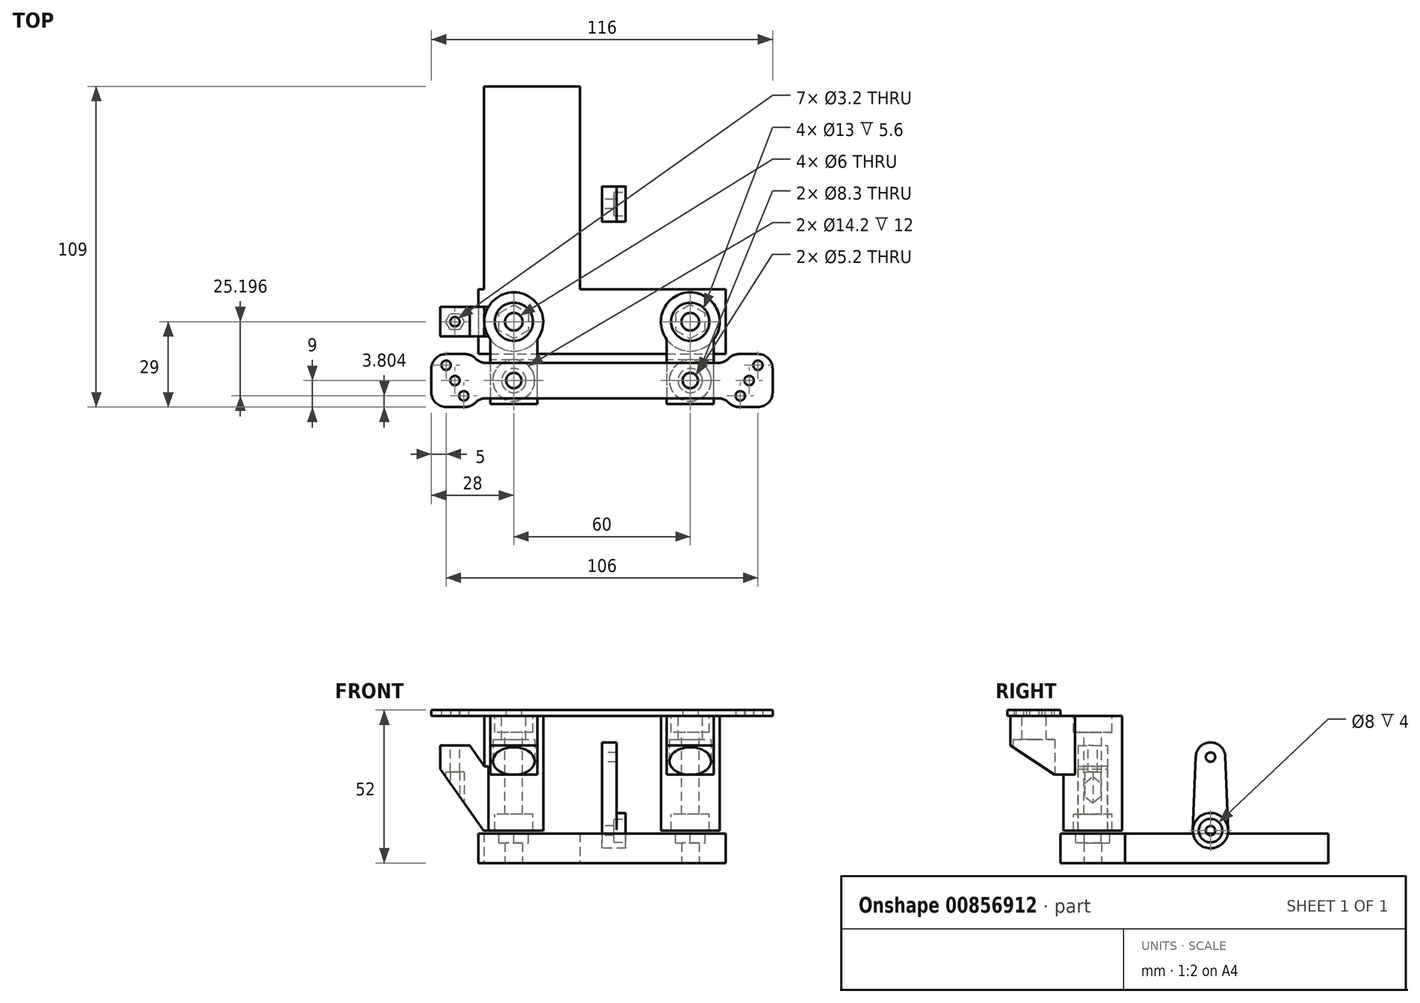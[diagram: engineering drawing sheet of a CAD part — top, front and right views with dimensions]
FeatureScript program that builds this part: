
annotation { "Feature Type Name" : "Feature", "Feature Type Description" : "" }
export const myFeature = defineFeature(function(context is Context, id is Id, definition is map)
    precondition{}
    {
        {
            var Q0;
            Q0=qCreatedBy(makeId("Top.planeOp"),FACE);
            var sketch = newSketch(context, id + "F0", { "sketchPlane" : qUnion([Q0])});
            skCircle(sketch, "E0", {"center": v(-30, 0) * mm, "radius": 3 * mm});
            skCircle(sketch, "E1", {"center": v(30, 0) * mm, "radius": 3 * mm});
            skLineSegment(sketch, "E2.bottom", {"start": v(-42, 11) * mm, "end": v(42, 11) * mm});
            skLineSegment(sketch, "E2.top", {"start": v(-42, -11) * mm, "end": v(42, -11) * mm});
            skLineSegment(sketch, "E2.left", {"start": v(-42, 11) * mm, "end": v(-42, -11) * mm});
            skLineSegment(sketch, "E2.right", {"start": v(42, 11) * mm, "end": v(42, -11) * mm});
            skPoint(sketch, "E2.middle", {"position": v(0, 0) * mm});
            skLineSegment(sketch, "E3", {"start": v(-30, 0) * mm, "end": v(30, 0) * mm, "construction": true});
            skSolve(sketch);
        }
        {
            var Q0;
            Q0 = qSketchRegion(id + "F0", true);
            extrude(context, id + "F1", {"entities" : qUnion([Q0]), "depth" : 10 * mm, "offsetDistance" : 25 * mm});
        }
        {
            var Q0;
            Q0=makeQuery(id+"F1.opExtrude","CAP_FACE",FACE,{"disambiguationData":[OSD([sQuery(id+"F0.wireOp",EDGE,"E0"),sQuery(id+"F0.wireOp",EDGE,"E1"),sQuery(id+"F0.wireOp",EDGE,"E2.bottom"),sQuery(id+"F0.wireOp",EDGE,"E2.top"),sQuery(id+"F0.wireOp",EDGE,"E2.left"),sQuery(id+"F0.wireOp",EDGE,"E2.right")])],"isStart":false});
            var sketch = newSketch(context, id + "F2", { "sketchPlane" : qUnion([Q0])});
            skCircle(sketch, "E4.cCircle", {"center": v(-30, 0) * mm, "radius": 5 * mm, "construction": true});
            skLineSegment(sketch, "E4.0", {"start": v(-25, 2.89) * mm, "end": v(-25, -2.89) * mm});
            skLineSegment(sketch, "E4.1", {"start": v(-25, -2.89) * mm, "end": v(-30, -5.77) * mm});
            skLineSegment(sketch, "E4.2", {"start": v(-30, -5.77) * mm, "end": v(-35, -2.89) * mm});
            skLineSegment(sketch, "E4.3", {"start": v(-35, -2.89) * mm, "end": v(-35, 2.89) * mm});
            skLineSegment(sketch, "E4.4", {"start": v(-35, 2.89) * mm, "end": v(-30, 5.77) * mm});
            skLineSegment(sketch, "E4.5", {"start": v(-30, 5.77) * mm, "end": v(-25, 2.89) * mm});
            skPoint(sketch, "E4.0.midPoint", {"position": v(-25, 0) * mm});
            skLineSegment(sketch, "E5", {"start": v(0, 0) * mm, "end": v(0, 13.19) * mm, "construction": true});
            skLineSegment(sketch, "E6.MirrorCS", {"start": v(25, -2.89) * mm, "end": v(30, -5.77) * mm});
            skLineSegment(sketch, "E7.MirrorCS", {"start": v(35, 2.89) * mm, "end": v(30, 5.77) * mm});
            skPoint(sketch, "E8.MirrorP", {"position": v(25, 0) * mm});
            skCircle(sketch, "E9.MirrorC", {"center": v(30, 0) * mm, "radius": 5 * mm, "construction": true});
            skLineSegment(sketch, "E10.MirrorCS", {"start": v(25, 2.89) * mm, "end": v(25, -2.89) * mm});
            skLineSegment(sketch, "E11.MirrorCS", {"start": v(30, -5.77) * mm, "end": v(35, -2.89) * mm});
            skLineSegment(sketch, "E12.MirrorCS", {"start": v(35, -2.89) * mm, "end": v(35, 2.89) * mm});
            skLineSegment(sketch, "E13.MirrorCS", {"start": v(30, 5.77) * mm, "end": v(25, 2.89) * mm});
            skSolve(sketch);
        }
        {
            var Q0;
            Q0 = qSketchRegion(id + "F2", true);
            extrude(context, id + "F3", {"entities" : qUnion([Q0]), "operationType" : NewBodyOperationType.REMOVE, "oppositeDirection" : true, "depth" : 3.2 * mm, "offsetDistance" : 25 * mm});
        }
        {
            var Q0;
            Q0=qCreatedBy(makeId("Front.planeOp"),FACE);
            var sketch = newSketch(context, id + "F4", { "sketchPlane" : qUnion([Q0])});
            skLineSegment(sketch, "E14", {"start": v(-30, 31.7) * mm, "end": v(-30, -19.85) * mm, "construction": true});
            skLineSegment(sketch, "E15", {"start": v(0, 0) * mm, "end": v(0, 44.27) * mm, "construction": true});
            skLineSegment(sketch, "E16.bottom", {"start": v(-40, 11) * mm, "end": v(-36.5, 11) * mm});
            skLineSegment(sketch, "E16.top", {"start": v(-40, 50) * mm, "end": v(-36.5, 50) * mm});
            skLineSegment(sketch, "E16.left", {"start": v(-40, 11) * mm, "end": v(-40, 50) * mm});
            skLineSegment(sketch, "E17.right", {"start": v(-36.5, 11) * mm, "end": v(-36.5, 16.6) * mm});
            skLineSegment(sketch, "E18", {"start": v(-33, 44.4) * mm, "end": v(-33, 16.6) * mm});
            skLineSegment(sketch, "E19.trimOffspring", {"start": v(-33, 16.6) * mm, "end": v(-36.5, 16.6) * mm});
            skLineSegment(sketch, "E20", {"start": v(-40, 30.5) * mm, "end": v(-16.74, 30.5) * mm, "construction": true});
            skLineSegment(sketch, "E21.MirrorCS", {"start": v(-33, 44.4) * mm, "end": v(-36.5, 44.4) * mm});
            skLineSegment(sketch, "E22.MirrorCS", {"start": v(-36.5, 50) * mm, "end": v(-36.5, 44.4) * mm});
            skSolve(sketch);
        }
        {
            var Q0;
            Q0=makeQuery(id+"F4.imprint","IMPRINT",FACE,{"disambiguationData":[TD([[makeQuery(id+"F4.imprint","IMPRINT",EDGE,{"derivedFrom":sQuery(id+"F4.wireOp",EDGE,"E16.bottom")}),1.0]])]});
            var Q1;
            Q1=sQuery(id+"F4.wireOp",EDGE,"E14");
            revolve(context, id + "F5", {"surfaceOperationType" : NewSurfaceOperationType.NEW, "entities" : qUnion([Q0]), "axis" : qUnion([Q1]), "revolveType" : RevolveType.FULL});
        }
        {
            var Q0;
            Q0=makeQuery(id+"F5.opRevolve","SWEPT_FACE",FACE,{"disambiguationData":[OSD([sQuery(id+"F4.wireOp",EDGE,"E16.top")])]});
            var sketch = newSketch(context, id + "F6", { "sketchPlane" : qUnion([Q0])});
            skArc(sketch, "E23.0", {"start": v(-38, -6) * mm, "mid": v(-30, -10) * mm, "end": v(-22, -6) * mm});
            skLineSegment(sketch, "E24", {"start": v(-38, -6) * mm, "end": v(-38, -28) * mm});
            skLineSegment(sketch, "E25", {"start": v(-38, -28) * mm, "end": v(-22, -28) * mm});
            skLineSegment(sketch, "E26", {"start": v(-22, -28) * mm, "end": v(-22, -6) * mm});
            skLineSegment(sketch, "E27", {"start": v(-30, 0) * mm, "end": v(-30, -20) * mm, "construction": true});
            skCircle(sketch, "E28", {"center": v(-30, -20) * mm, "radius": 4.15 * mm});
            skSolve(sketch);
        }
        {
            var Q0;
            Q0 = qSketchRegion(id + "F6", true);
            extrude(context, id + "F7", {"entities" : qUnion([Q0]), "operationType" : NewBodyOperationType.ADD, "oppositeDirection" : true, "depth" : 20 * mm, "offsetDistance" : 25 * mm});
        }
        {
            var Q0;
            Q0=makeQuery(id+"F7.opExtrude","CAP_EDGE",EDGE,{"disambiguationData":[OSD([sQuery(id+"F6.wireOp",EDGE,"E25")])],"isStart":false});
            chamfer(context, id + "F8", {"entities" : qUnion([Q0]), "chamferType" : ChamferType.TWO_OFFSETS, "width1" : 10 * mm, "oppositeDirection" : false, "width2" : 15 * mm, "tangentPropagation" : true});
        }
        {
            var Q0;
            Q0=makeQuery(id+"F7.opExtrude","CAP_FACE",FACE,{"disambiguationData":[OSD([sQuery(id+"F6.wireOp",EDGE,"E23.0"),sQuery(id+"F6.wireOp",EDGE,"E24"),sQuery(id+"F6.wireOp",EDGE,"E25"),sQuery(id+"F6.wireOp",EDGE,"E26"),sQuery(id+"F6.wireOp",EDGE,"E28")])],"isStart":false});
            var sketch = newSketch(context, id + "F9", { "sketchPlane" : qUnion([Q0])});
            skCircle(sketch, "E29.0", {"center": v(-30, 20) * mm, "radius": 4.15 * mm, "construction": true});
            skCircle(sketch, "E30.cCircle", {"center": v(-30, 20) * mm, "radius": 7.1 * mm});
            skLineSegment(sketch, "E30.0", {"start": v(-34.1, 27.1) * mm, "end": v(-25.9, 27.1) * mm, "construction": true});
            skLineSegment(sketch, "E30.1", {"start": v(-25.9, 27.1) * mm, "end": v(-21.8, 20) * mm, "construction": true});
            skLineSegment(sketch, "E30.2", {"start": v(-21.8, 20) * mm, "end": v(-25.9, 12.9) * mm, "construction": true});
            skLineSegment(sketch, "E30.3", {"start": v(-25.9, 12.9) * mm, "end": v(-34.1, 12.9) * mm, "construction": true});
            skLineSegment(sketch, "E30.4", {"start": v(-34.1, 12.9) * mm, "end": v(-38.2, 20) * mm, "construction": true});
            skLineSegment(sketch, "E30.5", {"start": v(-38.2, 20) * mm, "end": v(-34.1, 27.1) * mm, "construction": true});
            skPoint(sketch, "E30.0.midPoint", {"position": v(-30, 27.1) * mm});
            skSolve(sketch);
        }
        {
            var Q0;
            Q0 = qSketchRegion(id + "F9", true);
            extrude(context, id + "F10", {"entities" : qUnion([Q0]), "operationType" : NewBodyOperationType.REMOVE, "oppositeDirection" : true, "depth" : 12 * mm, "offsetDistance" : 25 * mm});
        }
        {
            var Q0;
            Q0=makeQuery(id+"F5.opRevolve","SWEPT_BODY",BODY,{"disambiguationData":[OSD([sQuery(id+"F4.wireOp",EDGE,"E16.bottom"),sQuery(id+"F4.wireOp",EDGE,"E16.top"),sQuery(id+"F4.wireOp",EDGE,"E16.left"),sQuery(id+"F4.wireOp",EDGE,"E17.right"),sQuery(id+"F4.wireOp",EDGE,"E18"),sQuery(id+"F4.wireOp",EDGE,"E19.trimOffspring"),sQuery(id+"F4.wireOp",EDGE,"E21.MirrorCS"),sQuery(id+"F4.wireOp",EDGE,"E22.MirrorCS")])]});
            transform(context, id + "F11", {"entities" : qUnion([Q0]), "transformType" : TransformType.TRANSLATION_3D, "dx" : 60 * mm, "dy" : 0 * mm, "dz" : 0 * mm, "makeCopy" : true});
        }
        {
            var Q0;
            Q0=makeQuery(id+"F11.opPattern","COPY",FACE,{"derivedFrom":makeQuery(id+"F7.boolean.opBoolean","MERGE",FACE,{"derivedFrom":[makeQuery(id+"F5.opRevolve","SWEPT_FACE",FACE,{"disambiguationData":[OSD([sQuery(id+"F4.wireOp",EDGE,"E16.top")])]}),makeQuery(id+"F7.opExtrude","CAP_FACE",FACE,{"disambiguationData":[OSD([sQuery(id+"F6.wireOp",EDGE,"E23.0"),sQuery(id+"F6.wireOp",EDGE,"E24"),sQuery(id+"F6.wireOp",EDGE,"E25"),sQuery(id+"F6.wireOp",EDGE,"E26"),sQuery(id+"F6.wireOp",EDGE,"E28")])],"isStart":true})]}),"instanceName":"1"});
            var sketch = newSketch(context, id + "F12", { "sketchPlane" : qUnion([Q0])});
            skLineSegment(sketch, "E31", {"start": v(-50, -20) * mm, "end": v(50, -20) * mm, "construction": true});
            skLineSegment(sketch, "E32", {"start": v(0, 0) * mm, "end": v(0, -26) * mm, "construction": true});
            skLineSegment(sketch, "E33.bottom", {"start": v(42, -26) * mm, "end": v(0, -26) * mm});
            skPoint(sketch, "E33.middle", {"position": v(0, -20) * mm});
            skLineSegment(sketch, "E34", {"start": v(47, -25.2) * mm, "end": v(53, -14.8) * mm, "construction": true});
            skPoint(sketch, "E34.endSnap0", {"position": v(38, -17) * mm});
            skLineSegment(sketch, "E35.bottom", {"start": v(58, -11) * mm, "end": v(42, -11) * mm});
            skLineSegment(sketch, "E35.top", {"start": v(58, -29) * mm, "end": v(42, -29) * mm});
            skLineSegment(sketch, "E35.right", {"start": v(42, -11) * mm, "end": v(42, -14) * mm});
            skPoint(sketch, "E35.middle", {"position": v(50, -20) * mm});
            skCircle(sketch, "E36", {"center": v(53, -14.8) * mm, "radius": 1.6 * mm});
            skCircle(sketch, "E37", {"center": v(50, -20) * mm, "radius": 1.6 * mm});
            skCircle(sketch, "E38", {"center": v(47, -25.2) * mm, "radius": 1.6 * mm});
            skLineSegment(sketch, "E39.trimOffspring", {"start": v(42, -14) * mm, "end": v(0, -14) * mm});
            skLineSegment(sketch, "E40.trimOffspring", {"start": v(42, -26) * mm, "end": v(42, -29) * mm});
            skLineSegment(sketch, "E41", {"start": v(58, -11) * mm, "end": v(58, -29) * mm});
            skCircle(sketch, "E42.MirrorC", {"center": v(-50, -20) * mm, "radius": 1.6 * mm});
            skLineSegment(sketch, "E43.MirrorCS", {"start": v(-58, -11) * mm, "end": v(-58, -29) * mm});
            skLineSegment(sketch, "E44.MirrorCS", {"start": v(-58, -11) * mm, "end": v(-42, -11) * mm});
            skLineSegment(sketch, "E45.MirrorCS", {"start": v(-58, -29) * mm, "end": v(-42, -29) * mm});
            skLineSegment(sketch, "E46.MirrorCS", {"start": v(-42, -14) * mm, "end": v(0, -14) * mm});
            skPoint(sketch, "E47.MirrorP", {"position": v(-38, -17) * mm});
            skCircle(sketch, "E48.MirrorC", {"center": v(-53, -14.8) * mm, "radius": 1.6 * mm});
            skLineSegment(sketch, "E49.MirrorCS", {"start": v(-42, -26) * mm, "end": v(-42, -29) * mm});
            skLineSegment(sketch, "E50.MirrorCS", {"start": v(-47, -25.2) * mm, "end": v(-53, -14.8) * mm, "construction": true});
            skLineSegment(sketch, "E51.MirrorCS", {"start": v(-42, -11) * mm, "end": v(-42, -14) * mm});
            skLineSegment(sketch, "E52.MirrorCS", {"start": v(50, -20) * mm, "end": v(-50, -20) * mm, "construction": true});
            skLineSegment(sketch, "E53.MirrorCS", {"start": v(-42, -26) * mm, "end": v(0, -26) * mm});
            skCircle(sketch, "E54.MirrorC", {"center": v(-47, -25.2) * mm, "radius": 1.6 * mm});
            skCircle(sketch, "E55.0", {"center": v(30, -20) * mm, "radius": 4.15 * mm, "construction": true});
            skCircle(sketch, "E56.0", {"center": v(-30, -20) * mm, "radius": 4.15 * mm, "construction": true});
            skCircle(sketch, "E57", {"center": v(-30, -20) * mm, "radius": 2.6 * mm});
            skCircle(sketch, "E58", {"center": v(30, -20) * mm, "radius": 2.6 * mm});
            skSolve(sketch);
        }
        {
            var Q0;
            Q0 = qSketchRegion(id + "F12", true);
            extrude(context, id + "F13", {"entities" : qUnion([Q0]), "depth" : 2 * mm, "offsetDistance" : 25 * mm});
        }
        {
            var Q0;
            Q0=makeQuery(id+"F13.opExtrude","SWEPT_EDGE",EDGE,{"disambiguationData":[OSD([sQuery(id+"F12.wireOp",EDGE,"E43.MirrorCS"),sQuery(id+"F12.wireOp",EDGE,"E45.MirrorCS")])]});
            var Q1;
            Q1=makeQuery(id+"F13.opExtrude","SWEPT_EDGE",EDGE,{"disambiguationData":[OSD([sQuery(id+"F12.wireOp",EDGE,"E45.MirrorCS"),sQuery(id+"F12.wireOp",EDGE,"E49.MirrorCS")])]});
            var Q2;
            Q2=makeQuery(id+"F13.opExtrude","SWEPT_EDGE",EDGE,{"disambiguationData":[OSD([sQuery(id+"F12.wireOp",EDGE,"E43.MirrorCS"),sQuery(id+"F12.wireOp",EDGE,"E44.MirrorCS")])]});
            var Q3;
            Q3=makeQuery(id+"F13.opExtrude","SWEPT_EDGE",EDGE,{"disambiguationData":[OSD([sQuery(id+"F12.wireOp",EDGE,"E44.MirrorCS"),sQuery(id+"F12.wireOp",EDGE,"E51.MirrorCS")])]});
            var Q4;
            Q4=makeQuery(id+"F13.opExtrude","SWEPT_EDGE",EDGE,{"disambiguationData":[OSD([sQuery(id+"F12.wireOp",EDGE,"E35.top"),sQuery(id+"F12.wireOp",EDGE,"E40.trimOffspring")])]});
            var Q5;
            Q5=makeQuery(id+"F13.opExtrude","SWEPT_EDGE",EDGE,{"disambiguationData":[OSD([sQuery(id+"F12.wireOp",EDGE,"E35.top"),sQuery(id+"F12.wireOp",EDGE,"E41")])]});
            var Q6;
            Q6=makeQuery(id+"F13.opExtrude","SWEPT_EDGE",EDGE,{"disambiguationData":[OSD([sQuery(id+"F12.wireOp",EDGE,"E35.bottom"),sQuery(id+"F12.wireOp",EDGE,"E35.right")])]});
            var Q7;
            Q7=makeQuery(id+"F13.opExtrude","SWEPT_EDGE",EDGE,{"disambiguationData":[OSD([sQuery(id+"F12.wireOp",EDGE,"E35.bottom"),sQuery(id+"F12.wireOp",EDGE,"E41")])]});
            fillet(context, id + "F14", {"entities" : qUnion([Q0, Q1, Q2, Q3, Q4, Q5, Q6, Q7]), "radius" : 5 * mm, "tangentPropagation" : true, "allowEdgeOverflow" : false});
        }
        {
            var Q0;
            Q0=makeQuery(id+"F14.opFillet","BLEND_EDGE",EDGE,{"blendedFrom":[makeQuery(id+"F13.opExtrude","SWEPT_EDGE",EDGE,{"disambiguationData":[OSD([sQuery(id+"F12.wireOp",EDGE,"E35.top"),sQuery(id+"F12.wireOp",EDGE,"E40.trimOffspring")])]}),makeQuery(id+"F13.opExtrude","SWEPT_FACE",FACE,{"disambiguationData":[OSD([sQuery(id+"F12.wireOp",EDGE,"E33.bottom"),sQuery(id+"F12.wireOp",EDGE,"E53.MirrorCS")])]})],"blendedInto":[makeQuery(id+"F13.opExtrude","SWEPT_FACE",FACE,{"disambiguationData":[OSD([sQuery(id+"F12.wireOp",EDGE,"E33.bottom"),sQuery(id+"F12.wireOp",EDGE,"E53.MirrorCS")])]})]});
            var Q1;
            Q1=makeQuery(id+"F14.opFillet","BLEND_EDGE",EDGE,{"blendedFrom":[makeQuery(id+"F13.opExtrude","SWEPT_EDGE",EDGE,{"disambiguationData":[OSD([sQuery(id+"F12.wireOp",EDGE,"E35.bottom"),sQuery(id+"F12.wireOp",EDGE,"E35.right")])]}),makeQuery(id+"F13.opExtrude","SWEPT_FACE",FACE,{"disambiguationData":[OSD([sQuery(id+"F12.wireOp",EDGE,"E39.trimOffspring"),sQuery(id+"F12.wireOp",EDGE,"E46.MirrorCS")])]})],"blendedInto":[makeQuery(id+"F13.opExtrude","SWEPT_FACE",FACE,{"disambiguationData":[OSD([sQuery(id+"F12.wireOp",EDGE,"E39.trimOffspring"),sQuery(id+"F12.wireOp",EDGE,"E46.MirrorCS")])]})]});
            var Q2;
            Q2=makeQuery(id+"F14.opFillet","BLEND_EDGE",EDGE,{"blendedFrom":[makeQuery(id+"F13.opExtrude","SWEPT_EDGE",EDGE,{"disambiguationData":[OSD([sQuery(id+"F12.wireOp",EDGE,"E44.MirrorCS"),sQuery(id+"F12.wireOp",EDGE,"E51.MirrorCS")])]}),makeQuery(id+"F13.opExtrude","SWEPT_FACE",FACE,{"disambiguationData":[OSD([sQuery(id+"F12.wireOp",EDGE,"E39.trimOffspring"),sQuery(id+"F12.wireOp",EDGE,"E46.MirrorCS")])]})],"blendedInto":[makeQuery(id+"F13.opExtrude","SWEPT_FACE",FACE,{"disambiguationData":[OSD([sQuery(id+"F12.wireOp",EDGE,"E39.trimOffspring"),sQuery(id+"F12.wireOp",EDGE,"E46.MirrorCS")])]})]});
            var Q3;
            Q3=makeQuery(id+"F14.opFillet","BLEND_EDGE",EDGE,{"blendedFrom":[makeQuery(id+"F13.opExtrude","SWEPT_EDGE",EDGE,{"disambiguationData":[OSD([sQuery(id+"F12.wireOp",EDGE,"E45.MirrorCS"),sQuery(id+"F12.wireOp",EDGE,"E49.MirrorCS")])]}),makeQuery(id+"F13.opExtrude","SWEPT_FACE",FACE,{"disambiguationData":[OSD([sQuery(id+"F12.wireOp",EDGE,"E33.bottom"),sQuery(id+"F12.wireOp",EDGE,"E53.MirrorCS")])]})],"blendedInto":[makeQuery(id+"F13.opExtrude","SWEPT_FACE",FACE,{"disambiguationData":[OSD([sQuery(id+"F12.wireOp",EDGE,"E33.bottom"),sQuery(id+"F12.wireOp",EDGE,"E53.MirrorCS")])]})]});
            fillet(context, id + "F15", {"entities" : qUnion([Q0, Q1, Q2, Q3]), "radius" : 5 * mm, "tangentPropagation" : true, "allowEdgeOverflow" : false});
        }
        {
            var Q0;
            Q0=qCreatedBy(makeId("Front.planeOp"),FACE);
            var sketch = newSketch(context, id + "F16", { "sketchPlane" : qUnion([Q0])});
            skLineSegment(sketch, "E59", {"start": v(-24, 40) * mm, "end": v(-76, 40) * mm, "construction": true});
            skLineSegment(sketch, "E60", {"start": v(-50, 40) * mm, "end": v(-50, 32) * mm, "construction": true});
            skLineSegment(sketch, "E61", {"start": v(-40, 11) * mm, "end": v(-40, 50) * mm, "construction": true});
            skLineSegment(sketch, "E62.bottom", {"start": v(-45, 40) * mm, "end": v(-55, 40) * mm});
            skLineSegment(sketch, "E62.top", {"start": v(-45, 32) * mm, "end": v(-55, 32) * mm, "construction": true});
            skLineSegment(sketch, "E62.left", {"start": v(-45, 40) * mm, "end": v(-45, 32) * mm, "construction": true});
            skLineSegment(sketch, "E62.right", {"start": v(-55, 40) * mm, "end": v(-55, 32) * mm});
            skPoint(sketch, "E62.middle", {"position": v(-50, 36) * mm});
            skLineSegment(sketch, "E63", {"start": v(-45, 40) * mm, "end": v(-40, 32.86) * mm});
            skLineSegment(sketch, "E64", {"start": v(-55, 32) * mm, "end": v(-40, 10.58) * mm});
            skPoint(sketch, "E65", {"position": v(-40, 30.5) * mm});
            skLineSegment(sketch, "E66", {"start": v(-40, 32.86) * mm, "end": v(-37, 32.86) * mm});
            skLineSegment(sketch, "E67", {"start": v(-37, 32.86) * mm, "end": v(-37, 11) * mm});
            skLineSegment(sketch, "E68", {"start": v(-37, 11) * mm, "end": v(-47.24, 11) * mm});
            skSolve(sketch);
        }
        {
            var Q0;
            Q0 = qSketchRegion(id + "F16", true);
            extrude(context, id + "F17", {"entities" : qUnion([Q0]), "operationType" : NewBodyOperationType.ADD, "depth" : 10 * mm, "offsetDistance" : 25 * mm, "symmetric" : true});
        }
        {
            var Q0;
            Q0=qCreatedBy(makeId("Right.planeOp"),FACE);
            var sketch = newSketch(context, id + "F18", { "sketchPlane" : qUnion([Q0])});
            skLineSegment(sketch, "E69", {"start": v(40, 11) * mm, "end": v(40, 36) * mm, "construction": true});
            skArc(sketch, "E70", {"start": v(45, 36.2) * mm, "mid": v(40, 41) * mm, "end": v(35, 36.2) * mm});
            skArc(sketch, "E71", {"start": v(34, 11.24) * mm, "mid": v(40, 5) * mm, "end": v(46, 11.24) * mm});
            skCircle(sketch, "E72", {"center": v(40, 36) * mm, "radius": 1.6 * mm});
            skLineSegment(sketch, "E73", {"start": v(46, 11.24) * mm, "end": v(45, 36.2) * mm});
            skLineSegment(sketch, "E74", {"start": v(35, 36.2) * mm, "end": v(34, 11.24) * mm});
            skCircle(sketch, "E75", {"center": v(40, 11) * mm, "radius": 1.6 * mm});
            skSolve(sketch);
        }
        {
            var Q0;
            Q0=makeQuery(id+"F18.imprint","IMPRINT",FACE,{"disambiguationData":[TD([[makeQuery(id+"F18.imprint","IMPRINT",EDGE,{"derivedFrom":sQuery(id+"F18.wireOp",EDGE,"E70")}),1.0]])]});
            extrude(context, id + "F19", {"entities" : qUnion([Q0]), "depth" : 5 * mm, "offsetDistance" : 25 * mm});
        }
        {
            var Q0;
            Q0=makeQuery(id+"F19.opExtrude","CAP_FACE",FACE,{"disambiguationData":[OSD([sQuery(id+"F18.wireOp",EDGE,"E70"),sQuery(id+"F18.wireOp",EDGE,"E71"),sQuery(id+"F18.wireOp",EDGE,"E72"),sQuery(id+"F18.wireOp",EDGE,"E73"),sQuery(id+"F18.wireOp",EDGE,"E74"),sQuery(id+"F18.wireOp",EDGE,"E75")])],"isStart":false});
            var sketch = newSketch(context, id + "F20", { "sketchPlane" : qUnion([Q0])});
            skCircle(sketch, "E76.0", {"center": v(40, 11) * mm, "radius": 1.6 * mm});
            skCircle(sketch, "E77", {"center": v(40, 11) * mm, "radius": 6 * mm});
            skSolve(sketch);
        }
        {
            var Q0;
            Q0 = qSketchRegion(id + "F20", true);
            extrude(context, id + "F21", {"entities" : qUnion([Q0]), "operationType" : NewBodyOperationType.ADD, "depth" : 3 * mm, "offsetDistance" : 25 * mm});
        }
        {
            var Q0;
            Q0=makeQuery(id+"F21.opExtrude","CAP_FACE",FACE,{"disambiguationData":[OSD([sQuery(id+"F20.wireOp",EDGE,"E76.0"),sQuery(id+"F20.wireOp",EDGE,"E77")])],"isStart":false});
            var sketch = newSketch(context, id + "F22", { "sketchPlane" : qUnion([Q0])});
            skCircle(sketch, "E78", {"center": v(40, 11) * mm, "radius": 4 * mm});
            skSolve(sketch);
        }
        {
            var Q0;
            Q0 = qSketchRegion(id + "F22", true);
            extrude(context, id + "F23", {"entities" : qUnion([Q0]), "operationType" : NewBodyOperationType.REMOVE, "oppositeDirection" : true, "depth" : 4 * mm, "offsetDistance" : 25 * mm});
        }
        {
            var Q0;
            Q0=makeQuery(id+"F17.boolean.opBoolean","MERGE",FACE,{"derivedFrom":[makeQuery(id+"F5.opRevolve","SWEPT_FACE",FACE,{"disambiguationData":[OSD([sQuery(id+"F4.wireOp",EDGE,"E16.bottom")])]}),makeQuery(id+"F17.opExtrude","SWEPT_FACE",FACE,{"disambiguationData":[OSD([sQuery(id+"F16.wireOp",EDGE,"E68")])]})]});
            var sketch = newSketch(context, id + "F24", { "sketchPlane" : qUnion([Q0])});
            skCircle(sketch, "E79.cCircle", {"center": v(-50, 0) * mm, "radius": 2.75 * mm, "construction": true});
            skLineSegment(sketch, "E79.0", {"start": v(-46.82, 0) * mm, "end": v(-48.41, -2.75) * mm});
            skLineSegment(sketch, "E79.1", {"start": v(-48.41, -2.75) * mm, "end": v(-51.59, -2.75) * mm});
            skLineSegment(sketch, "E79.2", {"start": v(-51.59, -2.75) * mm, "end": v(-53.18, 0) * mm});
            skLineSegment(sketch, "E79.3", {"start": v(-53.18, 0) * mm, "end": v(-51.59, 2.75) * mm});
            skLineSegment(sketch, "E79.4", {"start": v(-51.59, 2.75) * mm, "end": v(-48.41, 2.75) * mm});
            skLineSegment(sketch, "E79.5", {"start": v(-48.41, 2.75) * mm, "end": v(-46.82, 0) * mm});
            skPoint(sketch, "E79.0.midPoint", {"position": v(-47.62, -1.38) * mm});
            skLineSegment(sketch, "E80", {"start": v(-30, 0) * mm, "end": v(-50, 0) * mm, "construction": true});
            skSolve(sketch);
        }
        {
            var Q0;
            Q0 = qSketchRegion(id + "F24", true);
            extrude(context, id + "F25", {"entities" : qUnion([Q0]), "operationType" : NewBodyOperationType.REMOVE, "oppositeDirection" : true, "depth" : 20 * mm, "offsetDistance" : 25 * mm});
        }
        {
            var Q0;
            Q0=sQuery(id+"F24.wireOp",VERTEX,"E80.end");
            var Q1;
            Q1=makeQuery(id+"F5.opRevolve","SWEPT_BODY",BODY,{"disambiguationData":[OSD([sQuery(id+"F4.wireOp",EDGE,"E16.bottom"),sQuery(id+"F4.wireOp",EDGE,"E16.top"),sQuery(id+"F4.wireOp",EDGE,"E16.left"),sQuery(id+"F4.wireOp",EDGE,"E17.right"),sQuery(id+"F4.wireOp",EDGE,"E18"),sQuery(id+"F4.wireOp",EDGE,"E19.trimOffspring"),sQuery(id+"F4.wireOp",EDGE,"E21.MirrorCS"),sQuery(id+"F4.wireOp",EDGE,"E22.MirrorCS")])]});
            hole(context, id + "F26", {"style" : HoleStyle.SIMPLE, "endStyle" : HoleEndStyle.THROUGH, "holeDiameter" : 3.2 * mm, "majorDiameter" : 5 * mm, "isTappedThrough" : true, "tappedDepth" : 12 * mm, "tapClearance" : 3, "locations" : qUnion([Q0]), "scope" : qUnion([Q1])});
        }
        {
            var Q0;
            Q0=qCreatedBy(makeId("Top.planeOp"),FACE);
            var sketch = newSketch(context, id + "F27", { "sketchPlane" : qUnion([Q0])});
            skLineSegment(sketch, "E81", {"start": v(0, 53) * mm, "end": v(-62, 53) * mm, "construction": true});
            skLineSegment(sketch, "E82.bottom", {"start": v(-11.5, 73.5) * mm, "end": v(-50.5, 73.5) * mm, "construction": true});
            skLineSegment(sketch, "E82.top", {"start": v(-11.5, 32.5) * mm, "end": v(-50.5, 32.5) * mm, "construction": true});
            skLineSegment(sketch, "E82.left", {"start": v(-11.5, 73.5) * mm, "end": v(-11.5, 32.5) * mm, "construction": true});
            skLineSegment(sketch, "E82.right", {"start": v(-50.5, 73.5) * mm, "end": v(-50.5, 32.5) * mm, "construction": true});
            skPoint(sketch, "E82.middle", {"position": v(-31, 53) * mm});
            skLineSegment(sketch, "E83", {"start": v(-40.1, 80) * mm, "end": v(-40.1, 11) * mm});
            skLineSegment(sketch, "E84.0", {"start": v(-42, 11) * mm, "end": v(-42, -11) * mm});
            skLineSegment(sketch, "E85.0", {"start": v(-42, 11) * mm, "end": v(42, 11) * mm});
            skLineSegment(sketch, "E86", {"start": v(-7.5, 11) * mm, "end": v(-7.5, 80) * mm});
            skLineSegment(sketch, "E87", {"start": v(-40.1, 80) * mm, "end": v(-7.5, 80) * mm});
            skSolve(sketch);
        }
        {
            var Q0;
            {var subQ0=sQuery(id+"F27.wireOp",EDGE,"E83");Q0=makeQuery(id+"F27.imprint","IMPRINT",FACE,{"disambiguationData":[TD([[makeQuery(id+"F27.imprint","IMPRINT",EDGE,{"derivedFrom":subQ0}),1.0]])]});}
            var sketch = newSketch(context, id + "F28", { "sketchPlane" : qUnion([Q0])});
            skLineSegment(sketch, "E88.0", {"start": v(-40.1, 80) * mm, "end": v(-7.5, 80) * mm});
            skLineSegment(sketch, "E89.0", {"start": v(-7.5, 11) * mm, "end": v(-7.5, 80) * mm});
            skLineSegment(sketch, "E90.0", {"start": v(-40.1, 80) * mm, "end": v(-40.1, 11) * mm});
            skLineSegment(sketch, "E91.0", {"start": v(-40.1, 11) * mm, "end": v(-7.5, 11) * mm});
            skPoint(sketch, "E92.orphan", {"position": v(-42, 11) * mm});
            skPoint(sketch, "E93.orphan", {"position": v(42, 11) * mm});
            skSolve(sketch);
        }
        {
            var Q0;
            Q0 = qSketchRegion(id + "F28", true);
            extrude(context, id + "F29", {"entities" : qUnion([Q0]), "operationType" : NewBodyOperationType.ADD, "depth" : 10 * mm, "offsetDistance" : 25 * mm});
        }
    });
